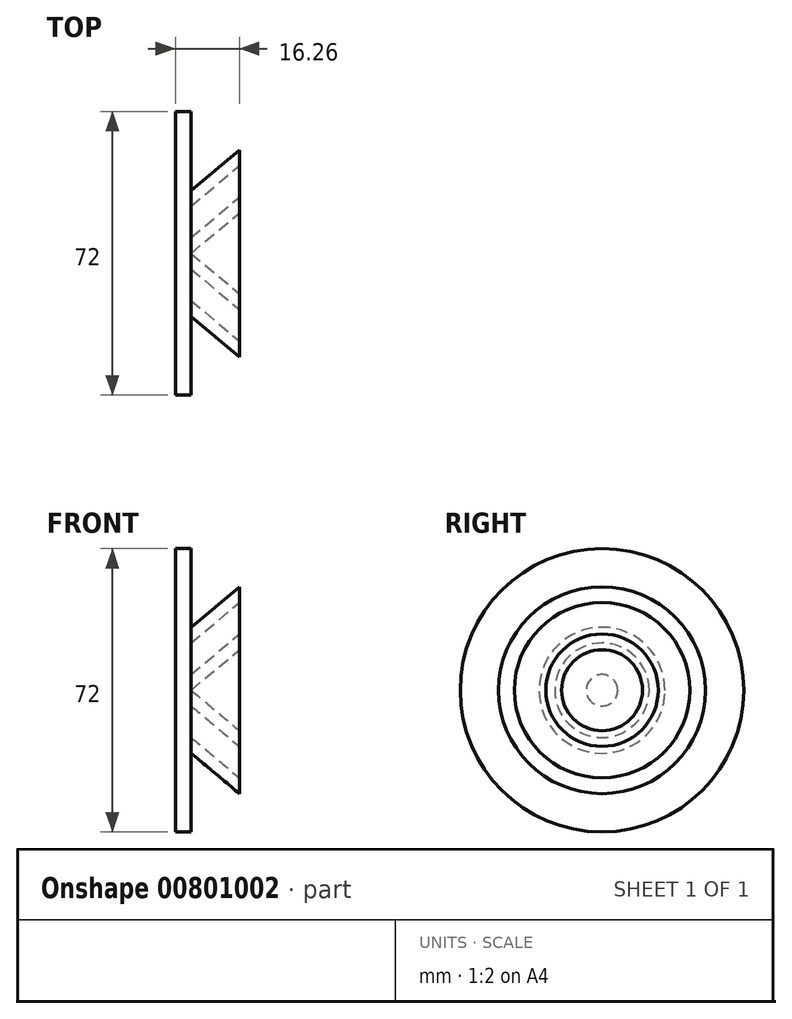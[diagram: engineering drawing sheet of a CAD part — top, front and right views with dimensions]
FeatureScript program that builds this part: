
annotation { "Feature Type Name" : "Feature", "Feature Type Description" : "" }
export const myFeature = defineFeature(function(context is Context, id is Id, definition is map)
    precondition{}
    {
        {
            var Q0;
            Q0=qCreatedBy(makeId("Top.planeOp"),FACE);
            var sketch = newSketch(context, id + "F0", { "sketchPlane" : qUnion([Q0])});
            skLineSegment(sketch, "E0", {"start": v(0, 0) * mm, "end": v(0, -36) * mm});
            skLineSegment(sketch, "E1", {"start": v(0, -36) * mm, "end": v(4, -36) * mm});
            skLineSegment(sketch, "E2", {"start": v(4, -36) * mm, "end": v(4, -16) * mm});
            skLineSegment(sketch, "E3", {"start": v(4, -16) * mm, "end": v(16.26, -26.28) * mm});
            skLineSegment(sketch, "E4", {"start": v(16.26, -26.28) * mm, "end": v(16.26, -22.28) * mm});
            skLineSegment(sketch, "E5", {"start": v(16.26, -22.28) * mm, "end": v(4, -12) * mm});
            skLineSegment(sketch, "E6", {"start": v(4, -12) * mm, "end": v(4, -4) * mm});
            skLineSegment(sketch, "E7", {"start": v(4, -4) * mm, "end": v(16.26, -14.28) * mm});
            skLineSegment(sketch, "E8", {"start": v(16.26, -14.28) * mm, "end": v(16.26, -10.28) * mm});
            skLineSegment(sketch, "E9", {"start": v(16.26, -10.28) * mm, "end": v(4, 0) * mm});
            skLineSegment(sketch, "E10", {"start": v(4, 0) * mm, "end": v(0, 0) * mm});
            skSolve(sketch);
        }
        {
            var Q0;
            Q0=makeQuery(id+"F0.imprint","IMPRINT",FACE,{"disambiguationData":[TD([[makeQuery(id+"F0.imprint","IMPRINT",EDGE,{"derivedFrom":sQuery(id+"F0.wireOp",EDGE,"E0")}),1.0]])]});
            var Q1;
            Q1=sQuery(id+"F0.wireOp",EDGE,"E10");
            revolve(context, id + "F1", {"surfaceOperationType" : NewSurfaceOperationType.NEW, "entities" : qUnion([Q0]), "axis" : qUnion([Q1]), "revolveType" : RevolveType.FULL});
        }
    });
